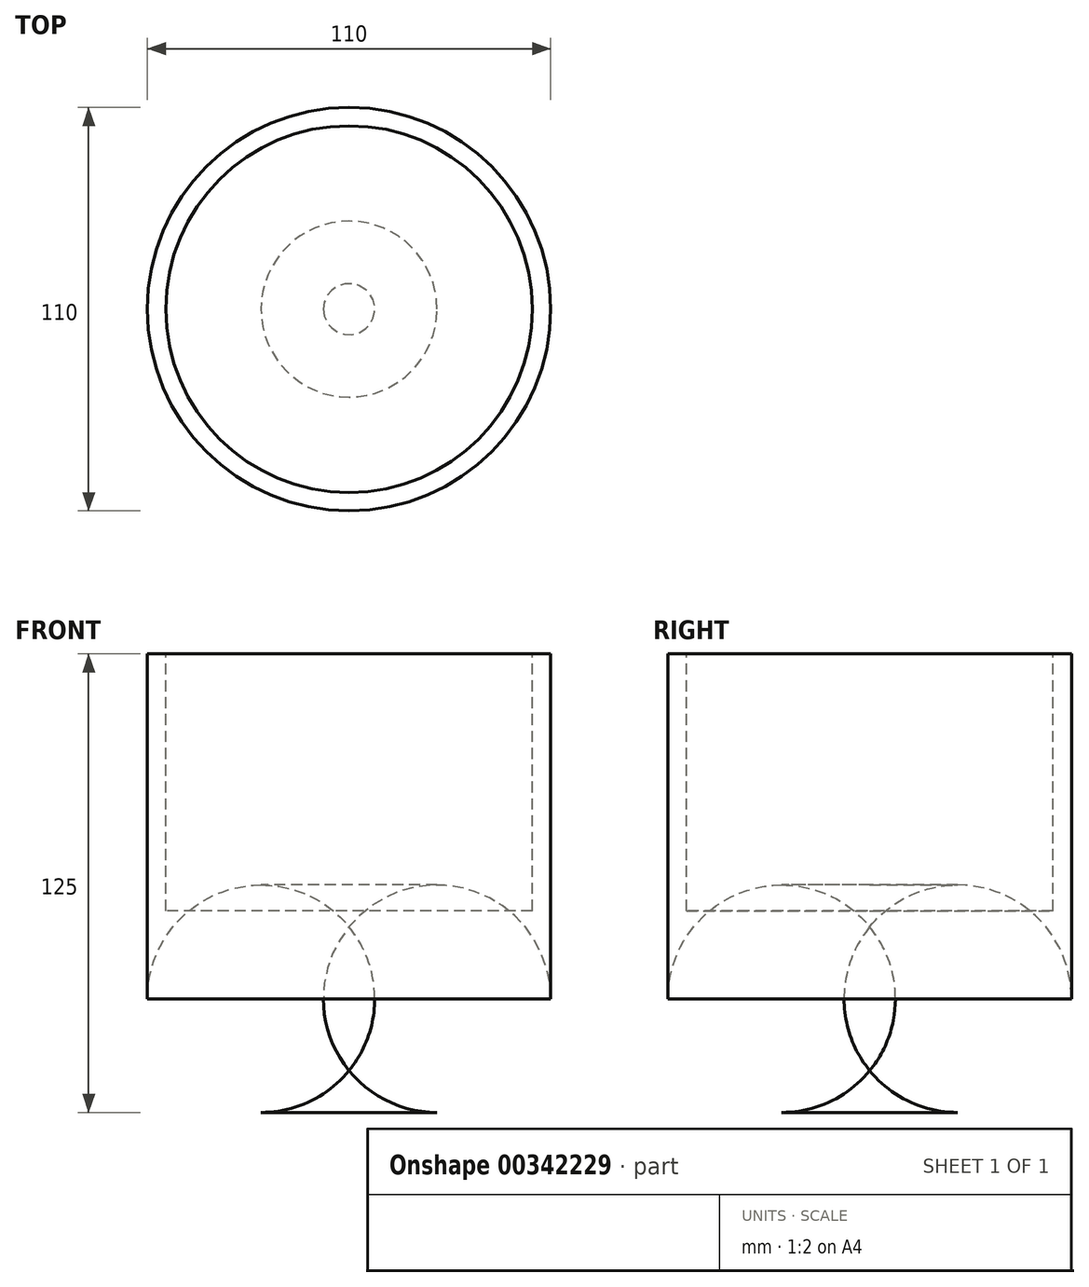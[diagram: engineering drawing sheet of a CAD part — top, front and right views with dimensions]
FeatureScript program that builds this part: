
annotation { "Feature Type Name" : "Feature", "Feature Type Description" : "" }
export const myFeature = defineFeature(function(context is Context, id is Id, definition is map)
    precondition{}
    {
        {
            var Q0;
            Q0=qCreatedBy(makeId("Top.planeOp"),FACE);
            var sketch = newSketch(context, id + "F0", { "sketchPlane" : qUnion([Q0])});
            skCircle(sketch, "E0", {"center": v(-64.8, -38.44) * mm, "radius": 55 * mm});
            skSolve(sketch);
        }
        {
            var Q0;
            Q0=makeQuery(id+"F0.imprint","IMPRINT",FACE,{"disambiguationData":[TD([[makeQuery(id+"F0.imprint","IMPRINT",EDGE,{"derivedFrom":sQuery(id+"F0.wireOp",EDGE,"E0")}),1.0]])]});
            extrude(context, id + "F1", {"entities" : qUnion([Q0]), "depth" : 100 * mm});
        }
        {
            var Q0;
            Q0=makeQuery(id+"F1.opExtrude","CAP_EDGE",EDGE,{"disambiguationData":[OSD([sQuery(id+"F0.wireOp",EDGE,"E0")])],"isStart":true});
            fillet(context, id + "F2", {"entities" : qUnion([Q0]), "radius" : 31 * mm, "tangentPropagation" : true, "allowEdgeOverflow" : false});
        }
        {
            var Q0;
            Q0=makeQuery(id+"F1.opExtrude","CAP_FACE",FACE,{"disambiguationData":[OSD([sQuery(id+"F0.wireOp",EDGE,"E0")])],"isStart":false});
            var sketch = newSketch(context, id + "F3", { "sketchPlane" : qUnion([Q0])});
            skCircle(sketch, "E1", {"center": v(-64.8, -38.44) * mm, "radius": 50 * mm});
            skSolve(sketch);
        }
        {
            var Q0;
            Q0 = qSketchRegion(id + "F3", true);
            extrude(context, id + "F4", {"entities" : qUnion([Q0]), "operationType" : NewBodyOperationType.REMOVE, "oppositeDirection" : true, "depth" : 70 * mm});
        }
        {
            var Q0;
            Q0=makeQuery(id+"F1.opExtrude","CAP_FACE",FACE,{"disambiguationData":[OSD([sQuery(id+"F0.wireOp",EDGE,"E0")])],"isStart":false});
            var Q1;
            Q1=makeQuery(id+"F4.boolean.opBoolean","COPY",FACE,{"derivedFrom":makeQuery(id+"F4.opExtrude","CAP_FACE",FACE,{"disambiguationData":[OSD([sQuery(id+"F3.wireOp",EDGE,"E1")])],"isStart":false})});
            extrude(context, id + "F5", {"entities" : qUnion([Q0, Q1]), "operationType" : NewBodyOperationType.ADD, "depth" : 25 * mm});
        }
    });
